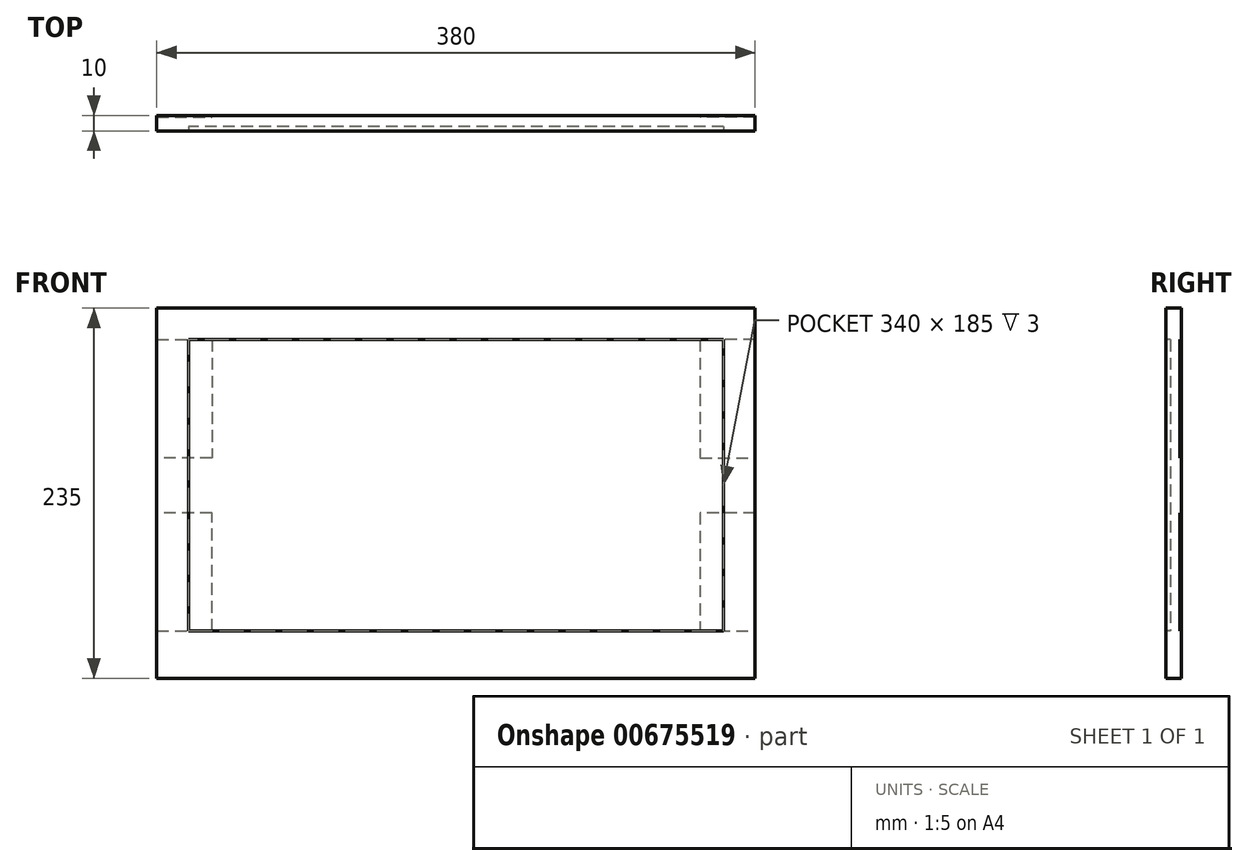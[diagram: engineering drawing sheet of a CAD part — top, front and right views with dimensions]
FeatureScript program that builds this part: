
annotation { "Feature Type Name" : "Feature", "Feature Type Description" : "" }
export const myFeature = defineFeature(function(context is Context, id is Id, definition is map)
    precondition{}
    {
        {
            var Q0;
            Q0=qCreatedBy(makeId("Front.planeOp"),FACE);
            var sketch = newSketch(context, id + "F0", { "sketchPlane" : qUnion([Q0])});
            skLineSegment(sketch, "E0.bottom", {"start": v(-190, 117.5) * mm, "end": v(190, 117.5) * mm});
            skLineSegment(sketch, "E0.top", {"start": v(-190, -117.5) * mm, "end": v(190, -117.5) * mm});
            skLineSegment(sketch, "E0.left", {"start": v(-190, 117.5) * mm, "end": v(-190, -117.5) * mm});
            skLineSegment(sketch, "E0.right", {"start": v(190, 117.5) * mm, "end": v(190, -117.5) * mm});
            skSolve(sketch);
        }
        {
            var Q0;
            Q0 = qSketchRegion(id + "F0", true);
            extrude(context, id + "F1", {"entities" : qUnion([Q0]), "depth" : 10 * mm, "offsetDistance" : 25 * mm});
        }
        {
            var Q0;
            Q0=makeQuery(id+"F1.opExtrude","CAP_FACE",FACE,{"disambiguationData":[OSD([sQuery(id+"F0.wireOp",EDGE,"E0.bottom"),sQuery(id+"F0.wireOp",EDGE,"E0.top"),sQuery(id+"F0.wireOp",EDGE,"E0.left"),sQuery(id+"F0.wireOp",EDGE,"E0.right")])],"isStart":false});
            var sketch = newSketch(context, id + "F2", { "sketchPlane" : qUnion([Q0])});
            skLineSegment(sketch, "E1.right", {"start": v(170, 97.5) * mm, "end": v(170, -87.5) * mm});
            skLineSegment(sketch, "E2", {"start": v(170, -87.5) * mm, "end": v(-170, -87.5) * mm});
            skLineSegment(sketch, "E3", {"start": v(170, 97.5) * mm, "end": v(-170, 97.5) * mm});
            skLineSegment(sketch, "E4", {"start": v(-170, -87.5) * mm, "end": v(-170, 97.5) * mm});
            skSolve(sketch);
        }
        {
            var Q0;
            Q0 = qSketchRegion(id + "F2", true);
            extrude(context, id + "F3", {"entities" : qUnion([Q0]), "operationType" : NewBodyOperationType.REMOVE, "oppositeDirection" : true, "depth" : 3 * mm, "offsetDistance" : 25 * mm});
        }
        {
            var Q0;
            Q0=makeQuery(id+"F1.opExtrude","CAP_FACE",FACE,{"disambiguationData":[OSD([sQuery(id+"F0.wireOp",EDGE,"E0.bottom"),sQuery(id+"F0.wireOp",EDGE,"E0.top"),sQuery(id+"F0.wireOp",EDGE,"E0.left"),sQuery(id+"F0.wireOp",EDGE,"E0.right")])],"isStart":true});
            var sketch = newSketch(context, id + "F4", { "sketchPlane" : qUnion([Q0])});
            skLineSegment(sketch, "E5", {"start": v(-190, 97.5) * mm, "end": v(-155, 97.5) * mm});
            skLineSegment(sketch, "E6", {"start": v(-155, 97.5) * mm, "end": v(-155, 22.5) * mm});
            skLineSegment(sketch, "E7", {"start": v(-155, 22.5) * mm, "end": v(-190, 22.5) * mm});
            skLineSegment(sketch, "E8", {"start": v(-190, -12.5) * mm, "end": v(-155, -12.5) * mm});
            skLineSegment(sketch, "E9", {"start": v(-155, -12.5) * mm, "end": v(-155, -87.5) * mm});
            skLineSegment(sketch, "E10", {"start": v(-155, -87.5) * mm, "end": v(-190, -87.5) * mm});
            skLineSegment(sketch, "E11", {"start": v(-190, 22.5) * mm, "end": v(-190, 97.5) * mm});
            skLineSegment(sketch, "E12", {"start": v(-190, -12.5) * mm, "end": v(-190, -87.5) * mm});
            skLineSegment(sketch, "E13", {"start": v(190, -87.5) * mm, "end": v(155, -87.5) * mm});
            skLineSegment(sketch, "E14", {"start": v(155, -87.5) * mm, "end": v(155, -12.5) * mm});
            skLineSegment(sketch, "E15", {"start": v(155, -12.5) * mm, "end": v(190, -12.5) * mm});
            skLineSegment(sketch, "E16", {"start": v(190, 97.5) * mm, "end": v(155, 97.5) * mm});
            skLineSegment(sketch, "E17", {"start": v(155, 97.5) * mm, "end": v(155, 22.5) * mm});
            skLineSegment(sketch, "E18", {"start": v(155, 22.5) * mm, "end": v(190, 22.5) * mm});
            skLineSegment(sketch, "E19", {"start": v(190, -87.5) * mm, "end": v(190, -12.5) * mm});
            skLineSegment(sketch, "E20", {"start": v(190, 22.5) * mm, "end": v(190, 97.5) * mm});
            skSolve(sketch);
        }
        {
            var Q0;
            Q0 = qSketchRegion(id + "F4", true);
            extrude(context, id + "F5", {"entities" : qUnion([Q0]), "operationType" : NewBodyOperationType.REMOVE, "oppositeDirection" : true, "depth" : 1 * mm, "offsetDistance" : 25 * mm});
        }
    });
